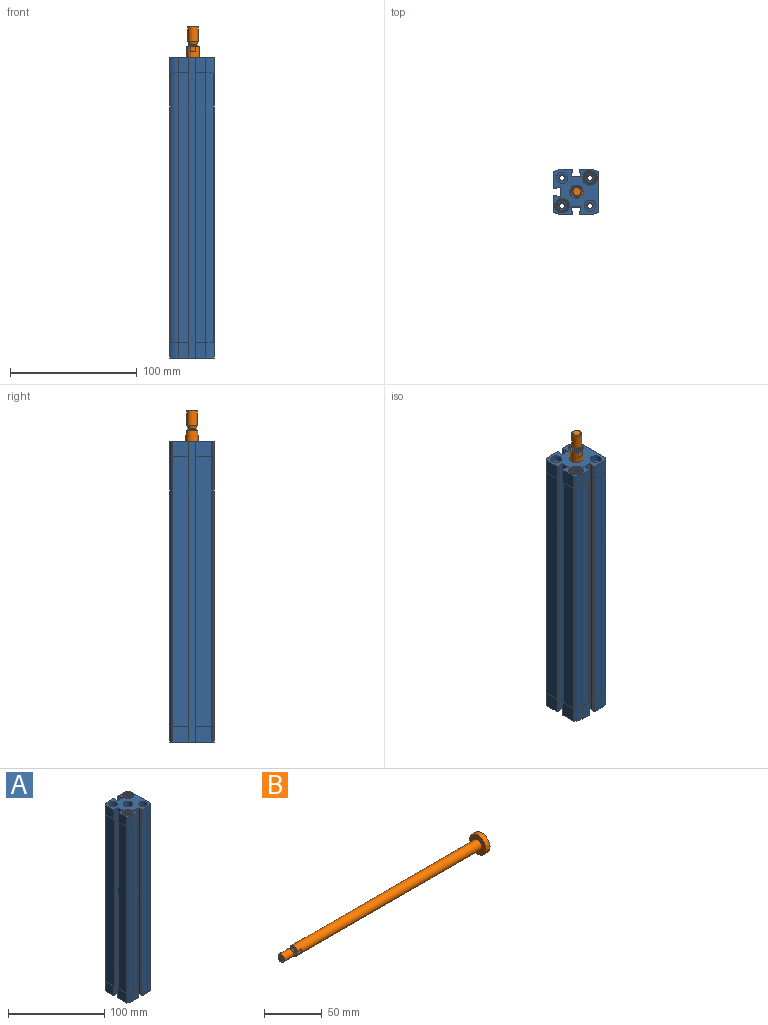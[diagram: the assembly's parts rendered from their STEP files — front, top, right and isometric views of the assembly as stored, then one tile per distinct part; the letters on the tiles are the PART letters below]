
ASSEMBLY  parts=2 mates=1
PART A: 334 faces, bbox 35.6x35.6x237.1 mm
  f0: plane 4.18x0.73mm, normal (1,0,0), area 2.6mm2, adj f1,f87,f88,f89
  f1: plane 4.18x0.64mm, normal (0.5,-0.87,0), area 2.6mm2, adj f0,f87,f88,f89
  f2: plane 4.18x0.64mm, normal (0.87,-0.5,0), area 2.6mm2, adj f87,f88,f92,f94
  f3: plane 4.18x0.64mm, normal (0.5,-0.87,0), area 2.6mm2, adj f4,f87,f88,f93
  f4: plane 4.18x0.64mm, normal (-0.5,-0.87,0), area 2.6mm2, adj f3,f87,f88,f93
  f5: plane 4.18x0.73mm, normal (0,-1,0), area 2.6mm2, adj f87,f88,f95,f97
  f6: plane 4.18x0.64mm, normal (-0.5,-0.87,0), area 2.6mm2, adj f7,f87,f88,f96
  f7: plane 4.18x0.73mm, normal (-1,0,0), area 2.6mm2, adj f6,f87,f88,f96
  f8: plane 4.18x0.64mm, normal (-0.87,-0.5,0), area 2.6mm2, adj f87,f88,f98,f100
  f9: plane 4.18x0.73mm, normal (-1,0,0), area 2.6mm2, adj f10,f87,f88,f99
  f10: plane 4.18x0.64mm, normal (-0.5,0.87,0), area 2.6mm2, adj f9,f87,f88,f99
  f11: plane 4.18x0.64mm, normal (-0.87,0.5,0), area 2.6mm2, adj f87,f88,f101,f103
  f12: plane 4.18x0.64mm, normal (-0.5,0.87,0), area 2.6mm2, adj f13,f87,f88,f102
  f13: plane 4.18x0.64mm, normal (0.5,0.87,0), area 2.6mm2, adj f12,f87,f88,f102
  f14: plane 4.18x0.73mm, normal (0,1,0), area 2.6mm2, adj f87,f88,f104,f106
  f15: plane 4.18x0.64mm, normal (0.5,0.87,0), area 2.6mm2, adj f16,f87,f88,f105
  f16: plane 4.18x0.73mm, normal (1,0,0), area 2.6mm2, adj f15,f87,f88,f105
  f17: plane 4.18x0.64mm, normal (0.87,0.5,0), area 2.6mm2, adj f87,f88,f90,f91
  f18: plane 4.18x0.73mm, normal (1,0,0), area 2.6mm2, adj f19,f113,f159,f160
  f19: plane 4.18x0.64mm, normal (0.5,-0.87,0), area 2.6mm2, adj f18,f113,f159,f160
  f20: plane 4.18x0.64mm, normal (0.87,-0.5,0), area 2.6mm2, adj f111,f112,f159,f160
  f21: plane 4.18x0.64mm, normal (0.5,-0.87,0), area 2.6mm2, adj f22,f110,f159,f160
  f22: plane 4.18x0.64mm, normal (-0.5,-0.87,0), area 2.6mm2, adj f21,f110,f159,f160
  f23: plane 4.18x0.73mm, normal (0,-1,0), area 2.6mm2, adj f108,f109,f159,f160
  f24: plane 4.18x0.64mm, normal (-0.5,-0.87,0), area 2.6mm2, adj f25,f107,f159,f160
  f25: plane 4.18x0.73mm, normal (-1,0,0), area 2.6mm2, adj f24,f107,f159,f160
  f26: plane 4.18x0.64mm, normal (-0.87,-0.5,0), area 2.6mm2, adj f123,f124,f159,f160
  f27: plane 4.18x0.73mm, normal (-1,0,0), area 2.6mm2, adj f28,f122,f159,f160
  f28: plane 4.18x0.64mm, normal (-0.5,0.87,0), area 2.6mm2, adj f27,f122,f159,f160
  f29: plane 4.18x0.64mm, normal (-0.87,0.5,0), area 2.6mm2, adj f120,f121,f159,f160
  f30: plane 4.18x0.64mm, normal (-0.5,0.87,0), area 2.6mm2, adj f31,f119,f159,f160
  f31: plane 4.18x0.64mm, normal (0.5,0.87,0), area 2.6mm2, adj f30,f119,f159,f160
  f32: plane 4.18x0.73mm, normal (0,1,0), area 2.6mm2, adj f117,f118,f159,f160
  f33: plane 4.18x0.64mm, normal (0.5,0.87,0), area 2.6mm2, adj f34,f116,f159,f160
  f34: plane 4.18x0.73mm, normal (1,0,0), area 2.6mm2, adj f33,f116,f159,f160
  f35: plane 4.18x0.64mm, normal (0.87,0.5,0), area 2.6mm2, adj f114,f115,f159,f160
  f36: plane 4.18x0.73mm, normal (1,0,0), area 2.6mm2, adj f37,f299,f300,f301
  f37: plane 4.18x0.64mm, normal (0.5,-0.87,0), area 2.6mm2, adj f36,f299,f300,f301
  f38: plane 4.18x0.64mm, normal (0.87,-0.5,0), area 2.6mm2, adj f299,f300,f303,f304
  f39: plane 4.18x0.64mm, normal (0.5,-0.87,0), area 2.6mm2, adj f40,f299,f300,f305
  f40: plane 4.18x0.64mm, normal (-0.5,-0.87,0), area 2.6mm2, adj f39,f299,f300,f305
  f41: plane 4.18x0.73mm, normal (0,-1,0), area 2.6mm2, adj f299,f300,f306,f307
  f42: plane 4.18x0.64mm, normal (-0.5,-0.87,0), area 2.6mm2, adj f43,f299,f300,f308
  f43: plane 4.18x0.73mm, normal (-1,0,0), area 2.6mm2, adj f42,f299,f300,f308
  f44: plane 4.18x0.64mm, normal (-0.87,-0.5,0), area 2.6mm2, adj f299,f300,f309,f310
  f45: plane 4.18x0.73mm, normal (-1,0,0), area 2.6mm2, adj f46,f299,f300,f311
  f46: plane 4.18x0.64mm, normal (-0.5,0.87,0), area 2.6mm2, adj f45,f299,f300,f311
  f47: plane 4.18x0.64mm, normal (-0.87,0.5,0), area 2.6mm2, adj f299,f300,f312,f313
  f48: plane 4.18x0.64mm, normal (-0.5,0.87,0), area 2.6mm2, adj f49,f299,f300,f314
  f49: plane 4.18x0.64mm, normal (0.5,0.87,0), area 2.6mm2, adj f48,f299,f300,f314
  f50: plane 4.18x0.73mm, normal (0,1,0), area 2.6mm2, adj f299,f300,f315,f316
  f51: plane 4.18x0.64mm, normal (0.5,0.87,0), area 2.6mm2, adj f52,f299,f300,f317
  f52: plane 4.18x0.73mm, normal (1,0,0), area 2.6mm2, adj f51,f299,f300,f317
  f53: plane 4.18x0.64mm, normal (0.87,0.5,0), area 2.6mm2, adj f299,f300,f302,f318
  f54: plane 4.18x0.73mm, normal (1,0,0), area 2.6mm2, adj f55,f72,f75,f76
  f55: plane 4.18x0.64mm, normal (0.5,-0.87,0), area 2.6mm2, adj f54,f72,f75,f76
  f56: plane 4.18x0.64mm, normal (0.87,-0.5,0), area 2.6mm2, adj f74,f75,f76,f319
  f57: plane 4.18x0.64mm, normal (0.5,-0.87,0), area 2.6mm2, adj f58,f75,f76,f320
  f58: plane 4.18x0.64mm, normal (-0.5,-0.87,0), area 2.6mm2, adj f57,f75,f76,f320
  f59: plane 4.18x0.73mm, normal (0,-1,0), area 2.6mm2, adj f75,f76,f321,f322
  f60: plane 4.18x0.64mm, normal (-0.5,-0.87,0), area 2.6mm2, adj f61,f75,f76,f323
  f61: plane 4.18x0.73mm, normal (-1,0,0), area 2.6mm2, adj f60,f75,f76,f323
  f62: plane 4.18x0.64mm, normal (-0.87,-0.5,0), area 2.6mm2, adj f75,f76,f324,f325
  f63: plane 4.18x0.73mm, normal (-1,0,0), area 2.6mm2, adj f64,f75,f76,f326
  f64: plane 4.18x0.64mm, normal (-0.5,0.87,0), area 2.6mm2, adj f63,f75,f76,f326
  f65: plane 4.18x0.64mm, normal (-0.87,0.5,0), area 2.6mm2, adj f75,f76,f327,f328
  f66: plane 4.18x0.64mm, normal (-0.5,0.87,0), area 2.6mm2, adj f67,f75,f76,f329
  f67: plane 4.18x0.64mm, normal (0.5,0.87,0), area 2.6mm2, adj f66,f75,f76,f329
  f68: plane 4.18x0.73mm, normal (0,1,0), area 2.6mm2, adj f75,f76,f330,f331
  f69: plane 4.18x0.64mm, normal (0.5,0.87,0), area 2.6mm2, adj f70,f75,f76,f332
  f70: plane 4.18x0.73mm, normal (1,0,0), area 2.6mm2, adj f69,f75,f76,f332
  f71: plane 4.18x0.64mm, normal (0.87,0.5,0), area 2.6mm2, adj f73,f75,f76,f333
  f72: plane 1.01x0.58mm, normal (0,0,-1), area 0.2mm2, adj f54,f55,f75
  f73: plane 1.17x0.34mm, normal (0,0,-1), area 0.2mm2, adj f71,f75,f333
  f74: plane 1.01x0.58mm, normal (0,0,-1), area 0.2mm2, adj f56,f75,f319
  f75: cylinder r=3.75mm len=7.5mm, axis (0,0,1), area 39.1mm2, adj f54,f55,f56,f57,f58,f59,f60,f61
  f76: cone r=3.75mm half-angle=30deg, axis (0,0,-1), area 18.3mm2, adj f54,f55,f56,f57,f58,f59,f60,f61
  f77: plane 7.5x7.5mm, normal (0,0,-1), area 24.5mm2, adj f75,f78
  f78: cone r=2.07mm half-angle=45deg, axis (0,0,-1), area 8.8mm2, adj f77,f294
  f79: cylinder r=2.07mm len=6.77mm, axis (0,0,1), area 87.9mm2, adj f145,f146
  f80: cylinder r=5.75mm len=11.5mm, axis (0,0,1), area 234.8mm2, adj f81,f178
  f81: plane 11.5x11.5mm, normal (0,0,-1), area 17.3mm2, adj f80,f166
  f82: cone r=5.25mm half-angle=45deg, axis (0,0,-1), area 17.9mm2, adj f83,f275
  f83: cylinder r=5.25mm len=10.5mm, axis (0,0,1), area 201.2mm2, adj f82,f274
  f84: cylinder r=2.07mm len=14.47mm, axis (0,0,1), area 187.9mm2, adj f85,f139
  f85: cone r=2.5mm half-angle=45deg, axis (0,0,1), area 8.8mm2, adj f84,f86
  f86: plane 7.5x7.5mm, normal (0,0,1), area 24.5mm2, adj f85,f87
  f87: cylinder r=3.75mm len=7.5mm, axis (0,0,1), area 39.1mm2, adj f0,f1,f2,f3,f4,f5,f6,f7
  f88: cone r=4.2mm half-angle=30deg, axis (0,0,1), area 18.3mm2, adj f0,f1,f2,f3,f4,f5,f6,f7
  f89: plane 1.01x0.58mm, normal (0,0,1), area 0.2mm2, adj f0,f1,f87
  f90: plane 4.18x0.64mm, normal (0.87,-0.5,0), area 2.6mm2, adj f17,f87,f88,f91
  f91: plane 1.17x0.34mm, normal (0,0,1), area 0.2mm2, adj f17,f87,f90
  f92: plane 1.01x0.58mm, normal (0,0,1), area 0.2mm2, adj f2,f87,f94
  f93: plane 1.17x0.34mm, normal (0,0,1), area 0.2mm2, adj f3,f4,f87
  f94: plane 4.18x0.73mm, normal (0,-1,0), area 2.6mm2, adj f2,f87,f88,f92
  f95: plane 1.01x0.58mm, normal (0,0,1), area 0.2mm2, adj f5,f87,f97
  f96: plane 1.01x0.58mm, normal (0,0,1), area 0.2mm2, adj f6,f7,f87
  f97: plane 4.18x0.64mm, normal (-0.87,-0.5,0), area 2.6mm2, adj f5,f87,f88,f95
  f98: plane 1.17x0.34mm, normal (0,0,1), area 0.2mm2, adj f8,f87,f100
  f99: plane 1.01x0.58mm, normal (0,0,1), area 0.2mm2, adj f9,f10,f87
  f100: plane 4.18x0.64mm, normal (-0.87,0.5,0), area 2.6mm2, adj f8,f87,f88,f98
  f101: plane 1.01x0.58mm, normal (0,0,1), area 0.2mm2, adj f11,f87,f103
  f102: plane 1.17x0.34mm, normal (0,0,1), area 0.2mm2, adj f12,f13,f87
  f103: plane 4.18x0.73mm, normal (0,1,0), area 2.6mm2, adj f11,f87,f88,f101
  f104: plane 1.01x0.58mm, normal (0,0,1), area 0.2mm2, adj f14,f87,f106
  f105: plane 1.01x0.58mm, normal (0,0,1), area 0.2mm2, adj f15,f16,f87
  f106: plane 4.18x0.64mm, normal (0.87,0.5,0), area 2.6mm2, adj f14,f87,f88,f104
  f107: plane 1.01x0.58mm, normal (0,0,1), area 0.2mm2, adj f24,f25,f159
  f108: plane 4.18x0.64mm, normal (-0.87,-0.5,0), area 2.6mm2, adj f23,f109,f159,f160
  f109: plane 1.01x0.58mm, normal (0,0,1), area 0.2mm2, adj f23,f108,f159
  f110: plane 1.17x0.34mm, normal (0,0,1), area 0.2mm2, adj f21,f22,f159
  f111: plane 4.18x0.73mm, normal (0,-1,0), area 2.6mm2, adj f20,f112,f159,f160
  f112: plane 1.01x0.58mm, normal (0,0,1), area 0.2mm2, adj f20,f111,f159
  f113: plane 1.01x0.58mm, normal (0,0,1), area 0.2mm2, adj f18,f19,f159
  f114: plane 4.18x0.64mm, normal (0.87,-0.5,0), area 2.6mm2, adj f35,f115,f159,f160
  f115: plane 1.17x0.34mm, normal (0,0,1), area 0.2mm2, adj f35,f114,f159
  f116: plane 1.01x0.58mm, normal (0,0,1), area 0.2mm2, adj f33,f34,f159
  f117: plane 4.18x0.64mm, normal (0.87,0.5,0), area 2.6mm2, adj f32,f118,f159,f160
  f118: plane 1.01x0.58mm, normal (0,0,1), area 0.2mm2, adj f32,f117,f159
  f119: plane 1.17x0.34mm, normal (0,0,1), area 0.2mm2, adj f30,f31,f159
  f120: plane 4.18x0.73mm, normal (0,1,0), area 2.6mm2, adj f29,f121,f159,f160
  f121: plane 1.01x0.58mm, normal (0,0,1), area 0.2mm2, adj f29,f120,f159
  f122: plane 1.01x0.58mm, normal (0,0,1), area 0.2mm2, adj f27,f28,f159
  f123: plane 4.18x0.64mm, normal (-0.87,0.5,0), area 2.6mm2, adj f26,f124,f159,f160
  f124: plane 1.17x0.34mm, normal (0,0,1), area 0.2mm2, adj f26,f123,f159
  f125: plane 5x5mm, normal (0,0,1), area 6.2mm2, adj f126,f298
  f126: cylinder r=2.5mm len=205.5mm, axis (0,0,1), area 3228mm2, adj f125,f127
  f127: plane 5x5mm, normal (0,0,-1), area 6.2mm2, adj f126,f156
  f128: plane 9x9mm, normal (0,0,-1), area 44mm2, adj f129,f130
  f129: cone r=2.07mm half-angle=45deg, axis (0,0,-1), area 8.8mm2, adj f128,f298
  f130: cylinder r=4.5mm len=9mm, axis (0,0,1), area 135.7mm2, adj f128,f178
  f131: plane 5x5mm, normal (0,0,1), area 6.2mm2, adj f132,f296
  f132: cylinder r=2.5mm len=205.5mm, axis (0,0,1), area 3228mm2, adj f131,f133
  f133: plane 5x5mm, normal (0,0,-1), area 6.2mm2, adj f132,f297
  f134: cone r=2.5mm half-angle=45deg, axis (0,0,1), area 8.8mm2, adj f135,f297
  f135: plane 9x9mm, normal (0,0,1), area 44mm2, adj f134,f136
  f136: cylinder r=4.5mm len=9mm, axis (0,0,1), area 135.7mm2, adj f135,f169
  f137: plane 5x5mm, normal (0,0,1), area 6.2mm2, adj f138,f295
  f138: cylinder r=2.5mm len=205.5mm, axis (0,0,1), area 3228mm2, adj f137,f139
  f139: plane 5x5mm, normal (0,0,-1), area 6.2mm2, adj f84,f138
  f140: plane 9x9mm, normal (0,0,-1), area 44mm2, adj f141,f142
  f141: cone r=2.07mm half-angle=45deg, axis (0,0,-1), area 8.8mm2, adj f140,f295
  f142: cylinder r=4.5mm len=9mm, axis (0,0,1), area 135.7mm2, adj f140,f178
  f143: plane 5x5mm, normal (0,0,1), area 6.2mm2, adj f144,f294
  f144: cylinder r=2.5mm len=205.5mm, axis (0,0,1), area 3228mm2, adj f143,f145
  f145: plane 5x5mm, normal (0,0,-1), area 6.2mm2, adj f79,f144
  f146: cone r=2.5mm half-angle=45deg, axis (0,0,1), area 8.8mm2, adj f79,f147
  f147: plane 9x9mm, normal (0,0,1), area 44mm2, adj f146,f148
  f148: cylinder r=4.5mm len=9mm, axis (0,0,1), area 135.7mm2, adj f147,f169
  f149: cylinder r=5.25mm len=10.5mm, axis (0,0,1), area 201.2mm2, adj f150,f163
  f150: cone r=4.85mm half-angle=45deg, axis (0,0,1), area 17.9mm2, adj f149,f151
  f151: plane 9.7x9.7mm, normal (0,0,-1), area 18.5mm2, adj f150,f299
  f152: plane 7.5x7.5mm, normal (0,0,-1), area 24.5mm2, adj f153,f300
  f153: cone r=2.07mm half-angle=45deg, axis (0,0,-1), area 8.8mm2, adj f152,f296
  f154: cone r=5.25mm half-angle=45deg, axis (0,0,-1), area 17.9mm2, adj f155,f161
  f155: cylinder r=5.25mm len=10.5mm, axis (0,0,1), area 201.2mm2, adj f154,f164
  f156: cylinder r=2.07mm len=14.47mm, axis (0,0,1), area 187.9mm2, adj f127,f157
  f157: cone r=2.5mm half-angle=45deg, axis (0,0,1), area 8.8mm2, adj f156,f158
  f158: plane 7.5x7.5mm, normal (0,0,1), area 24.5mm2, adj f157,f159
  f159: cylinder r=3.75mm len=7.5mm, axis (0,0,1), area 39.1mm2, adj f18,f19,f20,f21,f22,f23,f24,f25
  f160: cone r=4.2mm half-angle=30deg, axis (0,0,1), area 18.3mm2, adj f18,f19,f20,f21,f22,f23,f24,f25
  f161: plane 9.7x9.7mm, normal (0,0,1), area 18.5mm2, adj f154,f160
  f162: cylinder r=5.75mm len=11.5mm, axis (0,0,1), area 234.8mm2, adj f163,f178
  f163: plane 11.5x11.5mm, normal (0,0,-1), area 17.3mm2, adj f149,f162
  f164: plane 11.5x11.5mm, normal (0,0,1), area 17.3mm2, adj f155,f165
  f165: cylinder r=5.75mm len=11.5mm, axis (0,0,1), area 234.8mm2, adj f164,f169
  f166: cylinder r=5.25mm len=10.5mm, axis (0,0,1), area 201.2mm2, adj f81,f167
  f167: cone r=4.85mm half-angle=45deg, axis (0,0,1), area 17.9mm2, adj f166,f168
  f168: plane 9.7x9.7mm, normal (0,0,-1), area 18.5mm2, adj f76,f167
  f169: plane 35.5x35.5mm, normal (0,0,1), area 720.7mm2, adj f136,f148,f165,f179,f180,f181,f182,f183
  f170: cylinder r=0.4mm len=213mm, axis (0,0,-1), area 133.8mm2, adj f172,f220,f256,f257
  f171: plane 4.13x4.13mm, normal (1,0,0), area 13.4mm2, adj f262
  f172: plane 213x7.9mm, normal (0,-1,0), area 1682.7mm2, adj f170,f255,f256,f257
  f173: cylinder r=0.4mm len=213mm, axis (0,0,-1), area 133.8mm2, adj f174,f232,f259,f260
  f174: plane 213x7.9mm, normal (0,-1,0), area 1682.7mm2, adj f173,f175,f259,f260
  f175: cylinder r=12.75mm len=213mm, axis (0,0,-1), area 1350.3mm2, adj f174,f176,f259,f260
  f176: cylinder r=0.8mm len=213mm, axis (0,0,-1), area 182.9mm2, adj f175,f177,f259,f260
  f177: plane 213x12.15mm, normal (-1,0,0), area 2588.6mm2, adj f176,f259,f260,f261
  f178: plane 35.5x35.5mm, normal (0,0,-1), area 735.6mm2, adj f80,f130,f142,f162,f179,f180,f181,f182
  f179: plane 237x1.85mm, normal (0,1,0), area 385.2mm2, adj f169,f178,f180,f238,f241,f259,f260,f261
  f180: cylinder r=0.2mm len=237mm, axis (0,0,-1), area 74.5mm2, adj f169,f178,f179,f181
  f181: plane 237x0.3mm, normal (1,0,0), area 71.1mm2, adj f169,f178,f180,f182
  f182: cylinder r=0.2mm len=237mm, axis (0,0,-1), area 74.5mm2, adj f169,f178,f181,f183
  f183: plane 237x2.8mm, normal (0,1,0), area 663.6mm2, adj f169,f178,f182,f184
  f184: cylinder r=0.4mm len=237mm, axis (0,0,-1), area 148.9mm2, adj f169,f178,f183,f185
  f185: plane 237x6mm, normal (-1,0,0), area 1422mm2, adj f169,f178,f184,f186
  f186: cylinder r=0.4mm len=237mm, axis (0,0,-1), area 148.9mm2, adj f169,f178,f185,f187
  f187: plane 237x2.8mm, normal (0,-1,0), area 663.6mm2, adj f169,f178,f186,f188
  f188: cylinder r=0.2mm len=237mm, axis (0,0,-1), area 74.5mm2, adj f169,f178,f187,f189
  f189: plane 237x0.3mm, normal (1,0,0), area 71.1mm2, adj f169,f178,f188,f190
  f190: cylinder r=0.2mm len=237mm, axis (0,0,-1), area 74.5mm2, adj f169,f178,f189,f191
  f191: plane 237x1.85mm, normal (0,-1,0), area 385.2mm2, adj f169,f178,f190,f192,f242,f244,f258,f293
  f192: cylinder r=0.4mm len=12mm, axis (0,0,-1), area 7.5mm2, adj f169,f191,f193,f244
  f193: plane 12.26x12mm, normal (-1,0,0), area 147.2mm2, adj f169,f192,f194,f244
  f194: cylinder r=0.8mm len=12mm, axis (0,0,-1), area 10.1mm2, adj f169,f193,f195,f244
  f195: cylinder r=12.75mm len=12mm, axis (0,0,-1), area 79.7mm2, adj f169,f194,f196,f244
  f196: plane 12x7.9mm, normal (0,1,0), area 94.8mm2, adj f169,f195,f197,f244
  f197: cylinder r=0.4mm len=12mm, axis (0,0,-1), area 7.5mm2, adj f169,f196,f198,f244
  f198: plane 237x1.85mm, normal (1,0,0), area 385.2mm2, adj f169,f178,f197,f199,f243,f244,f258,f288
  f199: cylinder r=0.2mm len=237mm, axis (0,0,-1), area 74.5mm2, adj f169,f178,f198,f200
  f200: plane 237x0.3mm, normal (0,-1,0), area 71.1mm2, adj f169,f178,f199,f201
  f201: cylinder r=0.2mm len=237mm, axis (0,0,-1), area 74.5mm2, adj f169,f178,f200,f202
  f202: plane 237x2.8mm, normal (1,0,0), area 663.6mm2, adj f169,f178,f201,f203
  f203: cylinder r=0.4mm len=237mm, axis (0,0,-1), area 148.9mm2, adj f169,f178,f202,f204
  f204: plane 237x6mm, normal (0,1,0), area 1422mm2, adj f169,f178,f203,f205
  f205: cylinder r=0.4mm len=237mm, axis (0,0,-1), area 148.9mm2, adj f169,f178,f204,f206
  f206: plane 237x2.8mm, normal (-1,0,0), area 663.6mm2, adj f169,f178,f205,f207
  f207: cylinder r=0.2mm len=237mm, axis (0,0,-1), area 74.5mm2, adj f169,f178,f206,f208
  f208: plane 237x0.3mm, normal (0,-1,0), area 71.1mm2, adj f169,f178,f207,f209
  f209: cylinder r=0.2mm len=237mm, axis (0,0,-1), area 74.5mm2, adj f169,f178,f208,f210
  f210: plane 237x1.85mm, normal (-1,0,0), area 385.2mm2, adj f169,f178,f209,f211,f249,f256,f257,f287
  f211: cylinder r=0.4mm len=12mm, axis (0,0,-1), area 7.5mm2, adj f169,f210,f212,f256
  f212: plane 12x7.9mm, normal (0,1,0), area 94.8mm2, adj f169,f211,f213,f256
  f213: cylinder r=12.75mm len=12mm, axis (0,0,-1), area 79.7mm2, adj f169,f212,f214,f256
  f214: cylinder r=0.8mm len=12mm, axis (0,0,-1), area 10.1mm2, adj f169,f213,f215,f256
  f215: plane 30.73x12mm, normal (1,0,0), area 349.1mm2, adj f169,f214,f216,f256,f263
  f216: cylinder r=0.8mm len=12mm, axis (0,0,-1), area 10.1mm2, adj f169,f215,f217,f256
  f217: cylinder r=12.75mm len=12mm, axis (0,0,-1), area 79.7mm2, adj f169,f216,f218,f256
  f218: plane 12x7.9mm, normal (0,-1,0), area 94.8mm2, adj f169,f217,f219,f256
  f219: cylinder r=0.4mm len=12mm, axis (0,0,-1), area 7.5mm2, adj f169,f218,f220,f256
  f220: plane 237x1.85mm, normal (-1,0,0), area 385.2mm2, adj f169,f170,f178,f219,f221,f256,f257,f281
  f221: cylinder r=0.2mm len=237mm, axis (0,0,-1), area 74.5mm2, adj f169,f178,f220,f222
  f222: plane 237x0.3mm, normal (0,1,0), area 71.1mm2, adj f169,f178,f221,f223
  f223: cylinder r=0.2mm len=237mm, axis (0,0,-1), area 74.5mm2, adj f169,f178,f222,f224
  f224: plane 237x2.8mm, normal (-1,0,0), area 663.6mm2, adj f169,f178,f223,f225
  f225: cylinder r=0.4mm len=237mm, axis (0,0,-1), area 148.9mm2, adj f169,f178,f224,f226
  f226: plane 237x6mm, normal (0,-1,0), area 1422mm2, adj f169,f178,f225,f227
  f227: cylinder r=0.4mm len=237mm, axis (0,0,-1), area 148.9mm2, adj f169,f178,f226,f228
  f228: plane 237x2.8mm, normal (1,0,0), area 663.6mm2, adj f169,f178,f227,f229
  f229: cylinder r=0.2mm len=237mm, axis (0,0,-1), area 74.5mm2, adj f169,f178,f228,f230
  f230: plane 237x0.3mm, normal (0,1,0), area 71.1mm2, adj f169,f178,f229,f231
  f231: cylinder r=0.2mm len=237mm, axis (0,0,-1), area 74.5mm2, adj f169,f178,f230,f232
  f232: plane 237x1.85mm, normal (1,0,0), area 385.2mm2, adj f169,f173,f178,f231,f233,f259,f260,f282
  f233: cylinder r=0.4mm len=12mm, axis (0,0,-1), area 7.5mm2, adj f169,f232,f234,f260
  f234: plane 12x7.9mm, normal (0,-1,0), area 94.8mm2, adj f169,f233,f235,f260
  f235: cylinder r=12.75mm len=12mm, axis (0,0,-1), area 79.7mm2, adj f169,f234,f236,f260
  f236: cylinder r=0.8mm len=12mm, axis (0,0,-1), area 10.1mm2, adj f169,f235,f237,f260
  f237: plane 12.26x12mm, normal (-1,0,0), area 147.2mm2, adj f169,f236,f238,f260
  f238: cylinder r=0.4mm len=12mm, axis (0,0,-1), area 7.5mm2, adj f169,f179,f237,f260
  f239: plane 12.26x12mm, normal (-1,0,0), area 147.2mm2, adj f178,f240,f241,f259
  f240: cylinder r=0.8mm len=12mm, axis (0,0,-1), area 10.1mm2, adj f178,f239,f259,f284
  f241: cylinder r=0.4mm len=12mm, axis (0,0,-1), area 7.5mm2, adj f178,f179,f239,f259
  f242: cylinder r=0.4mm len=213mm, axis (0,0,-1), area 133.8mm2, adj f191,f244,f245,f258
  f243: cylinder r=0.4mm len=213mm, axis (0,0,-1), area 133.8mm2, adj f198,f244,f248,f258
  f244: plane 15.05x15.05mm, normal (0,0,-1), area 7mm2, adj f191,f192,f193,f194,f195,f196,f197,f198
  f245: plane 213x12.15mm, normal (-1,0,0), area 2588.6mm2, adj f242,f244,f246,f258
  f246: cylinder r=0.8mm len=213mm, axis (0,0,-1), area 182.9mm2, adj f244,f245,f247,f258
  f247: cylinder r=12.75mm len=213mm, axis (0,0,-1), area 1350.3mm2, adj f244,f246,f248,f258
  f248: plane 213x7.9mm, normal (0,1,0), area 1682.7mm2, adj f243,f244,f247,f258
  f249: cylinder r=0.4mm len=213mm, axis (0,0,-1), area 133.8mm2, adj f210,f250,f256,f257
  f250: plane 213x7.9mm, normal (0,1,0), area 1682.7mm2, adj f249,f251,f256,f257
  f251: cylinder r=12.75mm len=213mm, axis (0,0,-1), area 1350.3mm2, adj f250,f252,f256,f257
  f252: cylinder r=0.8mm len=213mm, axis (0,0,-1), area 182.9mm2, adj f251,f253,f256,f257
  f253: plane 213x30.51mm, normal (1,0,0), area 6497.8mm2, adj f252,f254,f256,f257
  f254: cylinder r=0.8mm len=213mm, axis (0,0,-1), area 182.9mm2, adj f253,f255,f256,f257
  f255: cylinder r=12.75mm len=213mm, axis (0,0,-1), area 1350.3mm2, adj f172,f254,f256,f257
  f256: plane 35.5x15.05mm, normal (0,0,-1), area 15.4mm2, adj f170,f172,f210,f211,f212,f213,f214,f215
  f257: plane 35.5x15.05mm, normal (0,0,1), area 15.4mm2, adj f170,f172,f210,f220,f249,f250,f251,f252
  f258: plane 15.05x15.05mm, normal (0,0,1), area 7mm2, adj f191,f198,f242,f243,f245,f246,f247,f248
  f259: plane 15.05x15.05mm, normal (0,0,1), area 7mm2, adj f173,f174,f175,f176,f177,f179,f232,f239
  f260: plane 15.05x15.05mm, normal (0,0,-1), area 7mm2, adj f173,f174,f175,f176,f177,f179,f232,f233
  f261: cylinder r=0.4mm len=213mm, axis (0,0,-1), area 133.8mm2, adj f177,f179,f259,f260
  f262: cylinder r=2.07mm len=7.07mm, axis (-1,0,0), area 91.8mm2, adj f171,f263
  f263: cone r=2.07mm half-angle=45deg, axis (1,0,0), area 8.8mm2, adj f215,f262
  f264: plane 4.13x4.13mm, normal (1,0,0), area 13.4mm2, adj f265
  f265: cylinder r=2.07mm len=10.57mm, axis (-1,0,0), area 137.2mm2, adj f264,f266
  f266: cone r=2.07mm half-angle=45deg, axis (1,0,0), area 8.8mm2, adj f265,f276
  f267: cylinder r=5mm len=20mm, axis (0,0,1), area 628.3mm2, adj f169,f268
  f268: plane 20x20mm, normal (0,0,-1), area 235.6mm2, adj f267,f269
  f269: cylinder r=10mm len=205mm, axis (0,0,1), area 12880.5mm2, adj f268,f270
  f270: plane 20x20mm, normal (0,0,1), area 314.2mm2, adj f269
  f271: plane 9x9mm, normal (0,0,-1), area 63.6mm2, adj f272
  f272: cylinder r=4.5mm len=9mm, axis (0,0,1), area 59.4mm2, adj f178,f271
  f273: cylinder r=5.75mm len=11.5mm, axis (0,0,1), area 234.8mm2, adj f169,f274
  f274: plane 11.5x11.5mm, normal (0,0,1), area 17.3mm2, adj f83,f273
  f275: plane 9.7x9.7mm, normal (0,0,1), area 18.5mm2, adj f82,f88
  f276: plane 30.73x12mm, normal (1,0,0), area 349.1mm2, adj f178,f257,f266,f277,f278
  f277: cylinder r=0.8mm len=12mm, axis (0,0,-1), area 10.1mm2, adj f178,f257,f276,f285
  f278: cylinder r=0.8mm len=12mm, axis (0,0,-1), area 10.1mm2, adj f178,f257,f276,f279
  f279: cylinder r=12.75mm len=12mm, axis (0,0,-1), area 79.7mm2, adj f178,f257,f278,f280
  f280: plane 12x7.9mm, normal (0,-1,0), area 94.8mm2, adj f178,f257,f279,f281
  f281: cylinder r=0.4mm len=12mm, axis (0,0,-1), area 7.5mm2, adj f178,f220,f257,f280
  f282: cylinder r=0.4mm len=12mm, axis (0,0,-1), area 7.5mm2, adj f178,f232,f259,f283
  f283: plane 12x7.9mm, normal (0,-1,0), area 94.8mm2, adj f178,f259,f282,f284
  f284: cylinder r=12.75mm len=12mm, axis (0,0,-1), area 79.7mm2, adj f178,f240,f259,f283
  f285: cylinder r=12.75mm len=12mm, axis (0,0,-1), area 79.7mm2, adj f178,f257,f277,f286
  f286: plane 12x7.9mm, normal (0,1,0), area 94.8mm2, adj f178,f257,f285,f287
  f287: cylinder r=0.4mm len=12mm, axis (0,0,-1), area 7.5mm2, adj f178,f210,f257,f286
  f288: cylinder r=0.4mm len=12mm, axis (0,0,-1), area 7.5mm2, adj f178,f198,f258,f289
  f289: plane 12x7.9mm, normal (0,1,0), area 94.8mm2, adj f178,f258,f288,f290
  f290: cylinder r=12.75mm len=12mm, axis (0,0,-1), area 79.7mm2, adj f178,f258,f289,f291
  f291: cylinder r=0.8mm len=12mm, axis (0,0,-1), area 10.1mm2, adj f178,f258,f290,f292
  f292: plane 12.26x12mm, normal (-1,0,0), area 147.2mm2, adj f178,f258,f291,f293
  f293: cylinder r=0.4mm len=12mm, axis (0,0,-1), area 7.5mm2, adj f178,f191,f258,f292
  f294: cylinder r=2.07mm len=14.47mm, axis (0,0,1), area 187.9mm2, adj f78,f143
  f295: cylinder r=2.07mm len=6.77mm, axis (0,0,1), area 87.9mm2, adj f137,f141
  f296: cylinder r=2.07mm len=14.47mm, axis (0,0,1), area 187.9mm2, adj f131,f153
  f297: cylinder r=2.07mm len=6.77mm, axis (0,0,1), area 87.9mm2, adj f133,f134
  f298: cylinder r=2.07mm len=6.77mm, axis (0,0,1), area 87.9mm2, adj f125,f129
  f299: cone r=3.75mm half-angle=30deg, axis (0,0,-1), area 18.3mm2, adj f36,f37,f38,f39,f40,f41,f42,f43
  f300: cylinder r=3.75mm len=7.5mm, axis (0,0,1), area 39.1mm2, adj f36,f37,f38,f39,f40,f41,f42,f43
  f301: plane 1.01x0.58mm, normal (0,0,-1), area 0.2mm2, adj f36,f37,f300
  f302: plane 1.17x0.34mm, normal (0,0,-1), area 0.2mm2, adj f53,f300,f318
  f303: plane 1.01x0.58mm, normal (0,0,-1), area 0.2mm2, adj f38,f300,f304
  f304: plane 4.18x0.73mm, normal (0,-1,0), area 2.6mm2, adj f38,f299,f300,f303
  f305: plane 1.17x0.34mm, normal (0,0,-1), area 0.2mm2, adj f39,f40,f300
  f306: plane 1.01x0.58mm, normal (0,0,-1), area 0.2mm2, adj f41,f300,f307
  f307: plane 4.18x0.64mm, normal (-0.87,-0.5,0), area 2.6mm2, adj f41,f299,f300,f306
  f308: plane 1.01x0.58mm, normal (0,0,-1), area 0.2mm2, adj f42,f43,f300
  f309: plane 1.17x0.34mm, normal (0,0,-1), area 0.2mm2, adj f44,f300,f310
  f310: plane 4.18x0.64mm, normal (-0.87,0.5,0), area 2.6mm2, adj f44,f299,f300,f309
  f311: plane 1.01x0.58mm, normal (0,0,-1), area 0.2mm2, adj f45,f46,f300
  f312: plane 1.01x0.58mm, normal (0,0,-1), area 0.2mm2, adj f47,f300,f313
  f313: plane 4.18x0.73mm, normal (0,1,0), area 2.6mm2, adj f47,f299,f300,f312
  f314: plane 1.17x0.34mm, normal (0,0,-1), area 0.2mm2, adj f48,f49,f300
  f315: plane 1.01x0.58mm, normal (0,0,-1), area 0.2mm2, adj f50,f300,f316
  f316: plane 4.18x0.64mm, normal (0.87,0.5,0), area 2.6mm2, adj f50,f299,f300,f315
  f317: plane 1.01x0.58mm, normal (0,0,-1), area 0.2mm2, adj f51,f52,f300
  f318: plane 4.18x0.64mm, normal (0.87,-0.5,0), area 2.6mm2, adj f53,f299,f300,f302
  f319: plane 4.18x0.73mm, normal (0,-1,0), area 2.6mm2, adj f56,f74,f75,f76
  f320: plane 1.17x0.34mm, normal (0,0,-1), area 0.2mm2, adj f57,f58,f75
  f321: plane 1.01x0.58mm, normal (0,0,-1), area 0.2mm2, adj f59,f75,f322
  f322: plane 4.18x0.64mm, normal (-0.87,-0.5,0), area 2.6mm2, adj f59,f75,f76,f321
  f323: plane 1.01x0.58mm, normal (0,0,-1), area 0.2mm2, adj f60,f61,f75
  f324: plane 1.17x0.34mm, normal (0,0,-1), area 0.2mm2, adj f62,f75,f325
  f325: plane 4.18x0.64mm, normal (-0.87,0.5,0), area 2.6mm2, adj f62,f75,f76,f324
  f326: plane 1.01x0.58mm, normal (0,0,-1), area 0.2mm2, adj f63,f64,f75
  f327: plane 1.01x0.58mm, normal (0,0,-1), area 0.2mm2, adj f65,f75,f328
  f328: plane 4.18x0.73mm, normal (0,1,0), area 2.6mm2, adj f65,f75,f76,f327
  f329: plane 1.17x0.34mm, normal (0,0,-1), area 0.2mm2, adj f66,f67,f75
  f330: plane 1.01x0.58mm, normal (0,0,-1), area 0.2mm2, adj f68,f75,f331
  f331: plane 4.18x0.64mm, normal (0.87,0.5,0), area 2.6mm2, adj f68,f75,f76,f330
  f332: plane 1.01x0.58mm, normal (0,0,-1), area 0.2mm2, adj f69,f70,f75
  f333: plane 4.18x0.64mm, normal (0.87,-0.5,0), area 2.6mm2, adj f71,f73,f75,f76
PART B: 16 faces, bbox 246.5x20x20 mm
  f0: plane 4.36x4.2mm, normal (0,-1,0), area 18.3mm2, adj f1,f2,f3
  f1: plane 4.36x0.5mm, normal (-0.87,-0.5,0), area 1.7mm2, adj f0,f2
  f2: cylinder r=5mm len=225.5mm, axis (-1,0,0), area 7044.7mm2, adj f0,f1,f3,f5,f14,f15
  f3: plane 10x9mm, normal (-1,0,0), area 32.6mm2, adj f0,f2,f13,f14
  f4: plane 20x20mm, normal (1,0,0), area 314.2mm2, adj f6
  f5: plane 20x20mm, normal (-1,0,0), area 235.6mm2, adj f2,f6
  f6: cylinder r=10mm len=20mm, axis (-1,0,0), area 314.2mm2, adj f4,f5
  f7: plane 6.47x6.47mm, normal (-1,0,0), area 32.8mm2, adj f8
  f8: cone r=3.23mm half-angle=45deg, axis (1,0,0), area 24.6mm2, adj f7,f9
  f9: cylinder r=4mm len=11.26mm, axis (-1,0,0), area 283mm2, adj f8,f10
  f10: cone r=4mm half-angle=20deg, axis (-1,0,0), area 56.6mm2, adj f9,f11
  f11: torus R=3.7mm, axis (1,0,0), area 4.1mm2, adj f10,f12
  f12: cylinder r=3.1mm len=6.2mm, axis (-1,0,0), area 15.5mm2, adj f11,f13
  f13: torus R=3.7mm, axis (1,0,0), area 19.6mm2, adj f3,f12
  f14: plane 4.36x4.2mm, normal (0,1,0), area 18.3mm2, adj f2,f3,f15
  f15: plane 4.36x0.5mm, normal (-0.87,0.5,0), area 1.7mm2, adj f2,f14
PLACE A t=(-0.74,0,-3.5)mm
PLACE B rot(axis=(0.71,0,-0.71),180deg) t=(0,0,0)mm
MATE fastened A.f169 <-> B.f2  axis (0,0,1) through (0,0,-3.5)mm
